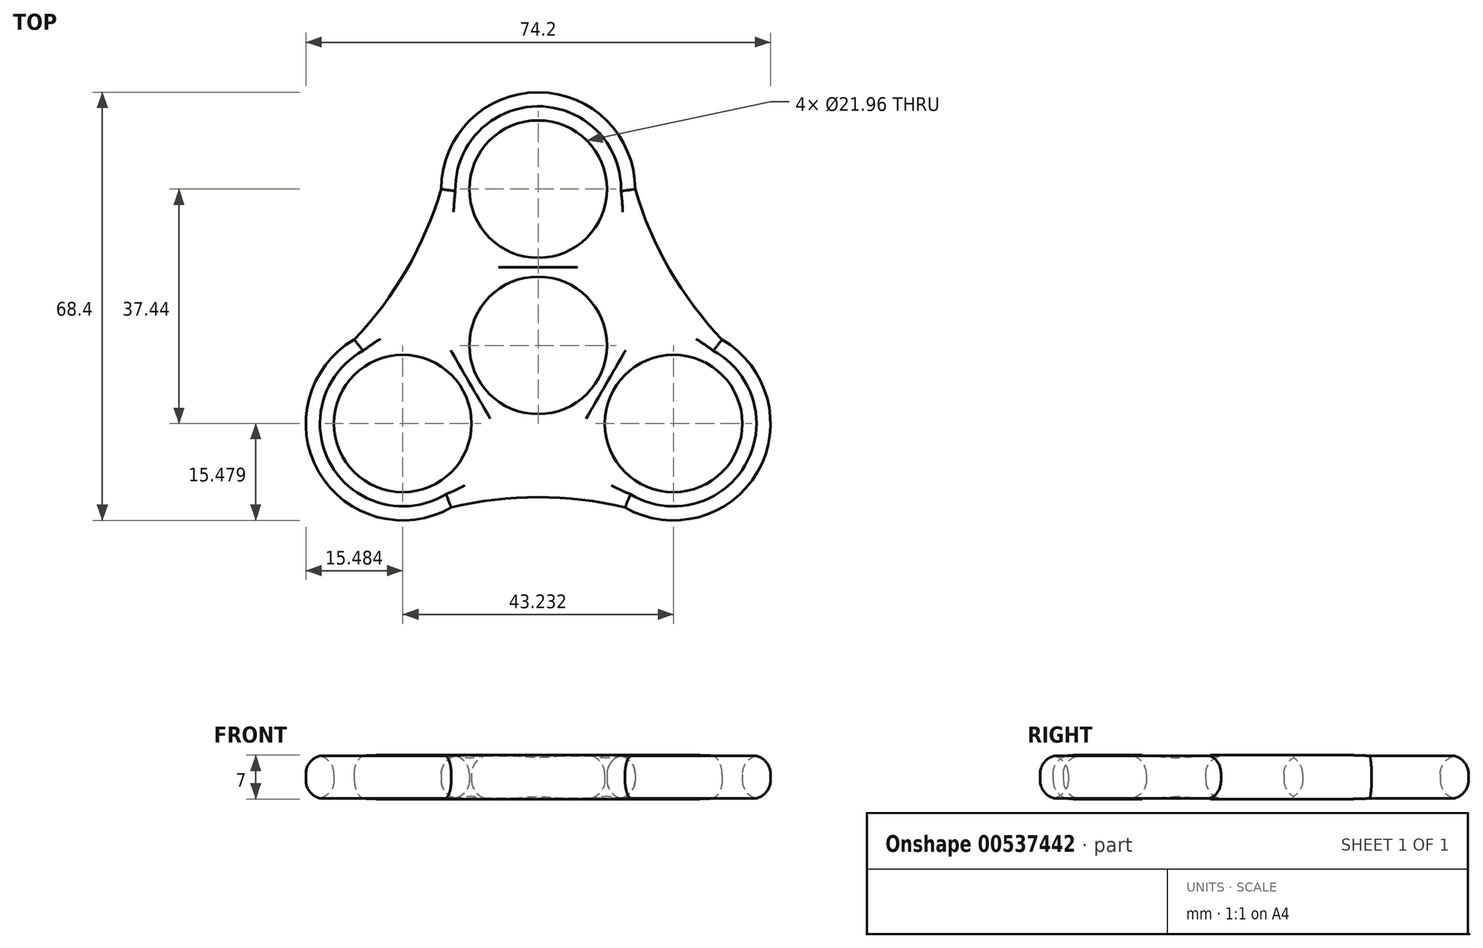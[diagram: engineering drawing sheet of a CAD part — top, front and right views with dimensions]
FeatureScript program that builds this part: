
annotation { "Feature Type Name" : "Feature", "Feature Type Description" : "" }
export const myFeature = defineFeature(function(context is Context, id is Id, definition is map)
    precondition{}
    {
        {
            var Q0;
            Q0=qCreatedBy(makeId("Top.planeOp"),FACE);
            var sketch = newSketch(context, id + "F0", { "sketchPlane" : qUnion([Q0])});
            skCircle(sketch, "E0", {"center": v(0, 39.15) * mm, "radius": 10.98 * mm});
            skCircle(sketch, "E1.1.0", {"center": v(-21.62, 1.7) * mm, "radius": 10.98 * mm});
            skCircle(sketch, "E1.2.0", {"center": v(21.62, 1.7) * mm, "radius": 10.98 * mm});
            skPoint(sketch, "E1.center", {"position": v(0, 14.19) * mm});
            skArc(sketch, "E2", {"start": v(15.48, 39.15) * mm, "mid": v(0, 54.63) * mm, "end": v(-15.48, 39.15) * mm});
            skArc(sketch, "E3.1.0", {"start": v(-29.36, 15.11) * mm, "mid": v(-35.02, -6.03) * mm, "end": v(-13.88, -11.7) * mm});
            skArc(sketch, "E3.2.0", {"start": v(13.88, -11.7) * mm, "mid": v(35.02, -6.03) * mm, "end": v(29.36, 15.11) * mm});
            skArc(sketch, "E4", {"start": v(-29.36, 15.11) * mm, "mid": v(-20.99, 26.3) * mm, "end": v(-15.48, 39.15) * mm});
            skArc(sketch, "E5", {"start": v(13.88, -11.7) * mm, "mid": v(0, -10.05) * mm, "end": v(-13.88, -11.7) * mm});
            skArc(sketch, "E6", {"start": v(15.48, 39.15) * mm, "mid": v(20.99, 26.3) * mm, "end": v(29.36, 15.11) * mm});
            skCircle(sketch, "E7", {"center": v(0, 14.19) * mm, "radius": 10.98 * mm});
            skSolve(sketch);
        }
        {
            var Q0;
            Q0 = qSketchRegion(id + "F0", true);
            extrude(context, id + "F1", {"entities" : qUnion([Q0]), "depth" : 7 * mm, "offsetDistance" : 25 * mm});
        }
        {
            var Q0;
            Q0=makeQuery(id+"F1.opExtrude","CAP_FACE",FACE,{"disambiguationData":[OSD([sQuery(id+"F0.wireOp",EDGE,"E0"),sQuery(id+"F0.wireOp",EDGE,"E1.1.0"),sQuery(id+"F0.wireOp",EDGE,"E1.2.0"),sQuery(id+"F0.wireOp",EDGE,"E2"),sQuery(id+"F0.wireOp",EDGE,"E3.1.0"),sQuery(id+"F0.wireOp",EDGE,"E3.2.0"),sQuery(id+"F0.wireOp",EDGE,"E4"),sQuery(id+"F0.wireOp",EDGE,"E5"),sQuery(id+"F0.wireOp",EDGE,"E6"),sQuery(id+"F0.wireOp",EDGE,"E7")])],"isStart":false});
            var Q1;
            Q1=makeQuery(id+"F1.opExtrude","CAP_FACE",FACE,{"disambiguationData":[OSD([sQuery(id+"F0.wireOp",EDGE,"E0"),sQuery(id+"F0.wireOp",EDGE,"E1.1.0"),sQuery(id+"F0.wireOp",EDGE,"E1.2.0"),sQuery(id+"F0.wireOp",EDGE,"E2"),sQuery(id+"F0.wireOp",EDGE,"E3.1.0"),sQuery(id+"F0.wireOp",EDGE,"E3.2.0"),sQuery(id+"F0.wireOp",EDGE,"E4"),sQuery(id+"F0.wireOp",EDGE,"E5"),sQuery(id+"F0.wireOp",EDGE,"E6"),sQuery(id+"F0.wireOp",EDGE,"E7")])],"isStart":true});
            fillet(context, id + "F2", {"entities" : qUnion([Q0, Q1]), "radius" : 3 * mm, "tangentPropagation" : true, "allowEdgeOverflow" : false});
        }
    });
